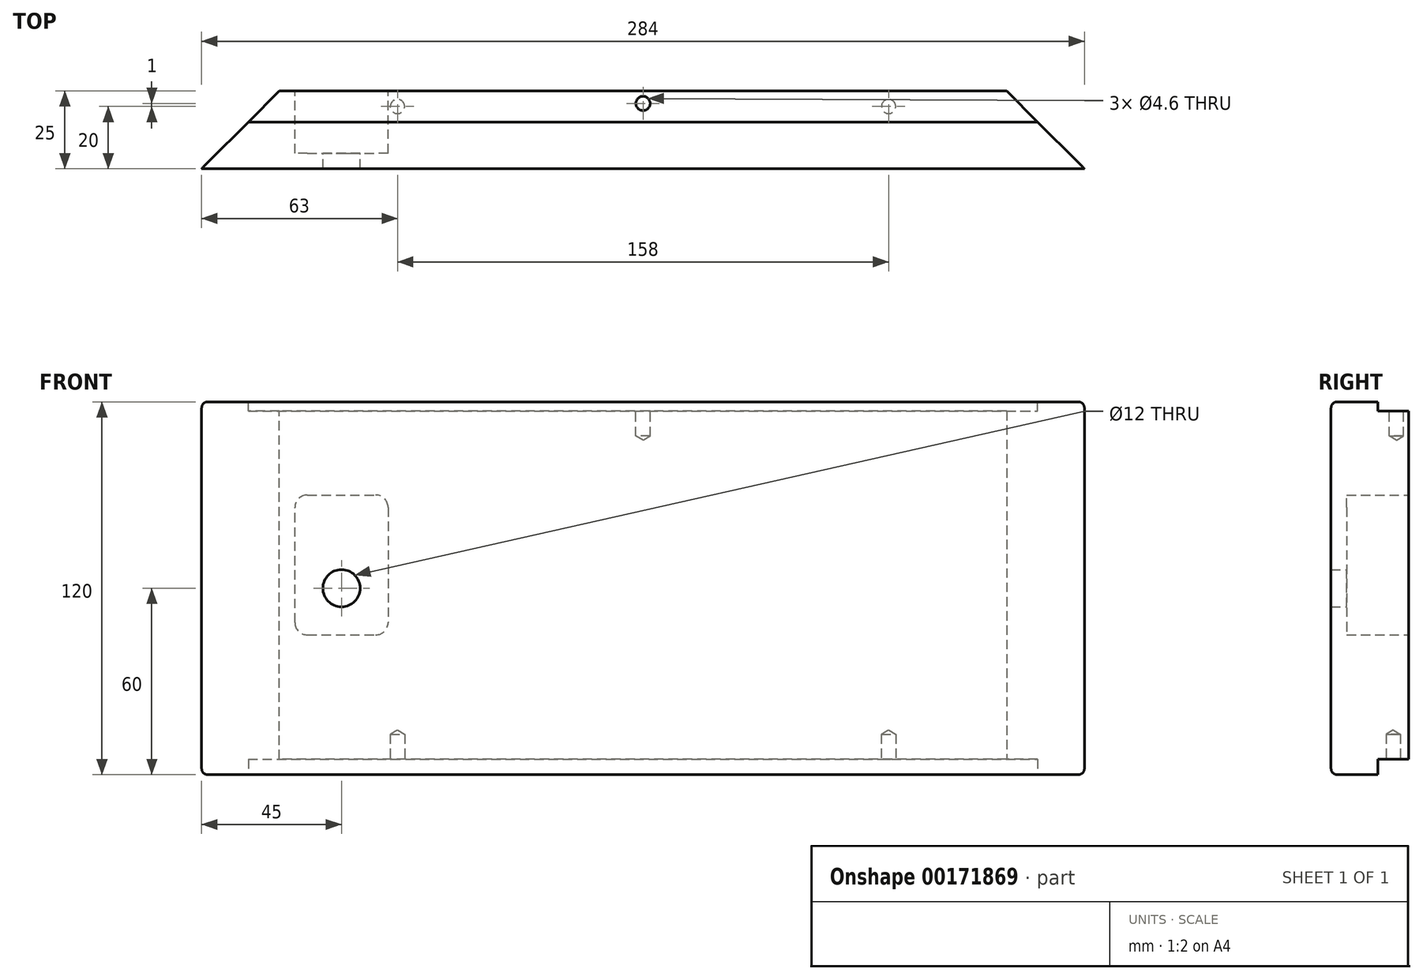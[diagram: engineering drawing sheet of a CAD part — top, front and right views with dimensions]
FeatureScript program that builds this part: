
annotation { "Feature Type Name" : "Feature", "Feature Type Description" : "" }
export const myFeature = defineFeature(function(context is Context, id is Id, definition is map)
    precondition{}
    {
        {
            var Q0;
            Q0=qCreatedBy(makeId("Front.planeOp"),FACE);
            var sketch = newSketch(context, id + "F0", { "sketchPlane" : qUnion([Q0])});
            skLineSegment(sketch, "E0.bottom", {"start": v(142, -60) * mm, "end": v(-142, -60) * mm});
            skLineSegment(sketch, "E0.top", {"start": v(142, 60) * mm, "end": v(-142, 60) * mm});
            skLineSegment(sketch, "E0.left", {"start": v(142, -60) * mm, "end": v(142, 60) * mm});
            skLineSegment(sketch, "E0.right", {"start": v(-142, -60) * mm, "end": v(-142, 60) * mm});
            skPoint(sketch, "E0.middle", {"position": v(0, 0) * mm});
            skLineSegment(sketch, "E1.right", {"start": v(-112, -11) * mm, "end": v(-112, 26) * mm});
            skLineSegment(sketch, "E2", {"start": v(-82, 26) * mm, "end": v(-82, -11) * mm});
            skLineSegment(sketch, "E3", {"start": v(-74.98, 0) * mm, "end": v(-115.97, 0) * mm, "construction": true});
            skLineSegment(sketch, "E4", {"start": v(-108, -15) * mm, "end": v(-86, -15) * mm});
            skLineSegment(sketch, "E5", {"start": v(-108, 30) * mm, "end": v(-86, 30) * mm});
            skPoint(sketch, "E6.visualSharp", {"position": v(-112, 30) * mm});
            skArc(sketch, "E6.filletArc", {"start": v(-108, 30) * mm, "mid": v(-110.83, 28.83) * mm, "end": v(-112, 26) * mm});
            skPoint(sketch, "E7.visualSharp", {"position": v(-82, 30) * mm});
            skArc(sketch, "E7.filletArc", {"start": v(-82, 26) * mm, "mid": v(-83.17, 28.83) * mm, "end": v(-86, 30) * mm});
            skPoint(sketch, "E8.visualSharp", {"position": v(-82, -15) * mm});
            skArc(sketch, "E8.filletArc", {"start": v(-86, -15) * mm, "mid": v(-83.17, -13.83) * mm, "end": v(-82, -11) * mm});
            skPoint(sketch, "E9.visualSharp", {"position": v(-112, -15) * mm});
            skArc(sketch, "E9.filletArc", {"start": v(-112, -11) * mm, "mid": v(-110.83, -13.83) * mm, "end": v(-108, -15) * mm});
            skLineSegment(sketch, "E10", {"start": v(-97, 45) * mm, "end": v(-97, -45) * mm, "construction": true});
            skLineSegment(sketch, "E11", {"start": v(-186.98, 0) * mm, "end": v(106.98, 0) * mm, "construction": true});
            skCircle(sketch, "E12", {"center": v(-97, 0) * mm, "radius": 6 * mm});
            skSolve(sketch);
        }
        {
            var Q0;
            Q0=makeQuery(id+"F0.imprint","IMPRINT",FACE,{"disambiguationData":[TD([[makeQuery(id+"F0.imprint","IMPRINT",EDGE,{"derivedFrom":sQuery(id+"F0.wireOp",EDGE,"E0.bottom")}),-1.0]])]});
            var Q1;
            Q1=makeQuery(id+"F0.imprint","IMPRINT",FACE,{"disambiguationData":[TD([[makeQuery(id+"F0.imprint","IMPRINT",EDGE,{"derivedFrom":sQuery(id+"F0.wireOp",EDGE,"E1.left")}),1.0]])]});
            var Q2;
            Q2=makeQuery(id+"F0.imprint","IMPRINT",FACE,{"disambiguationData":[TD([[makeQuery(id+"F0.imprint","IMPRINT",EDGE,{"derivedFrom":sQuery(id+"F0.wireOp",EDGE,"XVRcOiwa-wmZa-OlfB-imAZ-ZysaIvfTFvSH")}),1.0]])]});
            var Q3;
            Q3=makeQuery(id+"F0.imprint","IMPRINT",FACE,{"disambiguationData":[TD([[makeQuery(id+"F0.imprint","IMPRINT",EDGE,{"derivedFrom":sQuery(id+"F0.wireOp",EDGE,"492701c9-3a02-475b-877f-e4fc534a5983")}),1.0]])]});
            var Q4;
            Q4=makeQuery(id+"F0.imprint","IMPRINT",FACE,{"disambiguationData":[TD([[makeQuery(id+"F0.imprint","IMPRINT",EDGE,{"derivedFrom":sQuery(id+"F0.wireOp",EDGE,"E1.right")}),-1.0]])]});
            var Q5;
            {var subQ5=sQuery(id+"F0.wireOp",EDGE,"11b40b25-8dd5-4f7b-a4c1-55c3ff725173.left");Q5=makeQuery(id+"F0.imprint","IMPRINT",FACE,{"disambiguationData":[TD([[makeQuery(id+"F0.imprint","IMPRINT",EDGE,{"derivedFrom":subQ5}),1.0]])]});}
            var Q6;
            {var subQ0=sQuery(id+"F0.wireOp",EDGE,"050ddf37-6dd0-4eab-8f6c-0359ba11038c.filletArc");Q6=makeQuery(id+"F0.imprint","IMPRINT",FACE,{"disambiguationData":[TD([[makeQuery(id+"F0.imprint","IMPRINT",EDGE,{"derivedFrom":subQ0}),1.0]])]});}
            extrude(context, id + "F1", {"entities" : qUnion([Q0, Q1, Q2, Q3, Q4, Q5, Q6]), "depth" : 25 * mm});
        }
        {
            var Q0;
            Q0=makeQuery(id+"F1.opExtrude","CAP_EDGE",EDGE,{"disambiguationData":[OSD([sQuery(id+"F0.wireOp",EDGE,"E0.right")])],"isStart":true});
            var Q1;
            Q1=makeQuery(id+"F1.opExtrude","CAP_EDGE",EDGE,{"disambiguationData":[OSD([sQuery(id+"F0.wireOp",EDGE,"E0.left")])],"isStart":true});
            chamfer(context, id + "F2", {"entities" : qUnion([Q0, Q1]), "width" : 25 * mm, "tangentPropagation" : true});
        }
        {
            var Q0;
            Q0=makeQuery(id+"F1.opExtrude","SWEPT_FACE",FACE,{"disambiguationData":[OSD([sQuery(id+"F0.wireOp",EDGE,"E0.top")])]});
            var sketch = newSketch(context, id + "F3", { "sketchPlane" : qUnion([Q0])});
            skLineSegment(sketch, "E13", {"start": v(-127, -10) * mm, "end": v(127, -10) * mm});
            skLineSegment(sketch, "E14", {"start": v(-134.9, -4) * mm, "end": v(125.52, -4) * mm, "construction": true});
            skLineSegment(sketch, "E15", {"start": v(0, 10.75) * mm, "end": v(0, -16.45) * mm, "construction": true});
            skPoint(sketch, "E15.endSnap0", {"position": v(0, -10) * mm});
            skPoint(sketch, "E16", {"position": v(0, -4) * mm});
            skSolve(sketch);
        }
        {
            var Q0;
            {var subQ0=sQuery(id+"F3.wireOp",EDGE,"E13");Q0=makeQuery(id+"F3.imprint","IMPRINT",FACE,{"disambiguationData":[TD([[makeQuery(id+"F3.imprint","IMPRINT",EDGE,{"derivedFrom":subQ0}),1.0]])]});}
            extrude(context, id + "F4", {"entities" : qUnion([Q0]), "operationType" : NewBodyOperationType.REMOVE, "oppositeDirection" : true, "depth" : 3 * mm});
        }
        {
            var Q0;
            Q0=makeQuery(id+"F4.boolean.opBoolean","COPY",FACE,{"derivedFrom":makeQuery(id+"F4.opExtrude","CAP_FACE",FACE,{"disambiguationData":[OSD([sQuery(id+"F0.wireOp",EDGE,"E0.top"),sQuery(id+"F0.wireOp",EDGE,"E0.left"),sQuery(id+"F0.wireOp",EDGE,"E0.right"),sQuery(id+"F3.wireOp",EDGE,"E13")])],"isStart":false})});
            var sketch = newSketch(context, id + "F5", { "sketchPlane" : qUnion([Q0])});
            skLineSegment(sketch, "E17", {"start": v(-160.86, -4) * mm, "end": v(157.5, -4) * mm, "construction": true});
            skLineSegment(sketch, "E18", {"start": v(0, -19.46) * mm, "end": v(0, 5.76) * mm, "construction": true});
            skPoint(sketch, "E18.startSnap0", {"position": v(0, -10) * mm});
            skPoint(sketch, "E18.endSnap0", {"position": v(0, 0) * mm});
            skPoint(sketch, "E19", {"position": v(0, -4) * mm});
            skSolve(sketch);
        }
        {
            var Q0;
            Q0=sQuery(id+"F5.wireOp",VERTEX,"E19");
            var Q1;
            Q1=makeQuery(id+"F1.opExtrude","SWEPT_BODY",BODY,{"disambiguationData":[OSD([sQuery(id+"F0.wireOp",EDGE,"E0.bottom"),sQuery(id+"F0.wireOp",EDGE,"E0.top"),sQuery(id+"F0.wireOp",EDGE,"E0.left"),sQuery(id+"F0.wireOp",EDGE,"E0.right"),sQuery(id+"F0.wireOp",EDGE,"OmMS4I8q-v5Nw-sNs6-rLWv-C37PQFSncukl.bottom"),sQuery(id+"F0.wireOp",EDGE,"OmMS4I8q-v5Nw-sNs6-rLWv-C37PQFSncukl.top"),sQuery(id+"F0.wireOp",EDGE,"OmMS4I8q-v5Nw-sNs6-rLWv-C37PQFSncukl.left"),sQuery(id+"F0.wireOp",EDGE,"OmMS4I8q-v5Nw-sNs6-rLWv-C37PQFSncukl.right"),sQuery(id+"F0.wireOp",EDGE,"a599c4f8-9d5b-4f08-a6f5-21f0fa9e66a0.filletArc"),sQuery(id+"F0.wireOp",EDGE,"32fc2319-0cb2-45e8-9aa6-fcf55b2109a0.filletArc"),sQuery(id+"F0.wireOp",EDGE,"258bbff2-458d-4a09-ab05-362c01f2241a.filletArc"),sQuery(id+"F0.wireOp",EDGE,"b6ee52c4-7d80-4818-82dd-608125603be5.filletArc")])]});
            hole(context, id + "F6", {"style" : HoleStyle.SIMPLE, "endStyle" : HoleEndStyle.BLIND, "holeDiameter" : 4.6 * mm, "holeDepth" : 8 * mm, "startFromSketch" : true, "locations" : qUnion([Q0]), "scope" : qUnion([Q1])});
        }
        {
            var Q0;
            Q0=makeQuery(id+"F1.opExtrude","SWEPT_FACE",FACE,{"disambiguationData":[OSD([sQuery(id+"F0.wireOp",EDGE,"E0.bottom")])]});
            var sketch = newSketch(context, id + "F7", { "sketchPlane" : qUnion([Q0])});
            skLineSegment(sketch, "E20", {"start": v(-127, 10) * mm, "end": v(127, 10) * mm});
            skSolve(sketch);
        }
        {
            var Q0;
            {var subQ0=sQuery(id+"F7.wireOp",EDGE,"E20");Q0=makeQuery(id+"F7.imprint","IMPRINT",FACE,{"disambiguationData":[TD([[makeQuery(id+"F7.imprint","IMPRINT",EDGE,{"derivedFrom":subQ0}),-1.0]])]});}
            extrude(context, id + "F8", {"entities" : qUnion([Q0]), "operationType" : NewBodyOperationType.REMOVE, "oppositeDirection" : true, "depth" : 5 * mm});
        }
        {
            var Q0;
            Q0=makeQuery(id+"F8.boolean.opBoolean","COPY",FACE,{"derivedFrom":makeQuery(id+"F8.opExtrude","CAP_FACE",FACE,{"disambiguationData":[OSD([sQuery(id+"F0.wireOp",EDGE,"E0.bottom"),sQuery(id+"F0.wireOp",EDGE,"E0.left"),sQuery(id+"F0.wireOp",EDGE,"E0.right"),sQuery(id+"F7.wireOp",EDGE,"E20")])],"isStart":false})});
            var sketch = newSketch(context, id + "F9", { "sketchPlane" : qUnion([Q0])});
            skLineSegment(sketch, "E21", {"start": v(-269.27, 5) * mm, "end": v(258.64, 5) * mm, "construction": true});
            skLineSegment(sketch, "E22", {"start": v(-79, 26.7) * mm, "end": v(-79, -18.52) * mm, "construction": true});
            skLineSegment(sketch, "E23", {"start": v(79, 29.82) * mm, "end": v(79, -15.76) * mm, "construction": true});
            skPoint(sketch, "E24", {"position": v(-79, 5) * mm});
            skPoint(sketch, "E25", {"position": v(79, 5) * mm});
            skPoint(sketch, "E26", {"position": v(0, 5) * mm});
            skSolve(sketch);
        }
        {
            var Q0;
            Q0=sQuery(id+"F9.wireOp",VERTEX,"E24");
            var Q1;
            Q1=sQuery(id+"F9.wireOp",VERTEX,"E25");
            var Q2;
            Q2=makeQuery(id+"F1.opExtrude","SWEPT_BODY",BODY,{"disambiguationData":[OSD([sQuery(id+"F0.wireOp",EDGE,"E0.bottom"),sQuery(id+"F0.wireOp",EDGE,"E0.top"),sQuery(id+"F0.wireOp",EDGE,"E0.left"),sQuery(id+"F0.wireOp",EDGE,"E0.right"),sQuery(id+"F0.wireOp",EDGE,"OmMS4I8q-v5Nw-sNs6-rLWv-C37PQFSncukl.bottom"),sQuery(id+"F0.wireOp",EDGE,"OmMS4I8q-v5Nw-sNs6-rLWv-C37PQFSncukl.top"),sQuery(id+"F0.wireOp",EDGE,"OmMS4I8q-v5Nw-sNs6-rLWv-C37PQFSncukl.left"),sQuery(id+"F0.wireOp",EDGE,"OmMS4I8q-v5Nw-sNs6-rLWv-C37PQFSncukl.right"),sQuery(id+"F0.wireOp",EDGE,"a599c4f8-9d5b-4f08-a6f5-21f0fa9e66a0.filletArc"),sQuery(id+"F0.wireOp",EDGE,"32fc2319-0cb2-45e8-9aa6-fcf55b2109a0.filletArc"),sQuery(id+"F0.wireOp",EDGE,"258bbff2-458d-4a09-ab05-362c01f2241a.filletArc"),sQuery(id+"F0.wireOp",EDGE,"b6ee52c4-7d80-4818-82dd-608125603be5.filletArc")])]});
            hole(context, id + "F10", {"style" : HoleStyle.SIMPLE, "endStyle" : HoleEndStyle.BLIND, "holeDiameter" : 4.6 * mm, "holeDepth" : 8 * mm, "startFromSketch" : true, "locations" : qUnion([Q0, Q1]), "scope" : qUnion([Q2])});
        }
        {
            var Q0;
            Q0=makeQuery(id+"F1.opExtrude","CAP_EDGE",EDGE,{"disambiguationData":[OSD([sQuery(id+"F0.wireOp",EDGE,"E0.top")])],"isStart":false});
            var Q1;
            Q1=makeQuery(id+"F1.opExtrude","CAP_EDGE",EDGE,{"disambiguationData":[OSD([sQuery(id+"F0.wireOp",EDGE,"E0.bottom")])],"isStart":false});
            fillet(context, id + "F11", {"entities" : qUnion([Q0, Q1]), "radius" : 2 * mm, "tangentPropagation" : true, "allowEdgeOverflow" : false});
        }
        {
            var Q0;
            Q0=makeQuery(id+"F0.imprint","IMPRINT",FACE,{"disambiguationData":[TD([[makeQuery(id+"F0.imprint","IMPRINT",EDGE,{"derivedFrom":sQuery(id+"F0.wireOp",EDGE,"E1.left")}),1.0]])]});
            var Q1;
            Q1=makeQuery(id+"F0.imprint","IMPRINT",FACE,{"disambiguationData":[TD([[makeQuery(id+"F0.imprint","IMPRINT",EDGE,{"derivedFrom":sQuery(id+"F0.wireOp",EDGE,"XVRcOiwa-wmZa-OlfB-imAZ-ZysaIvfTFvSH")}),1.0]])]});
            var Q2;
            Q2=makeQuery(id+"F0.imprint","IMPRINT",FACE,{"disambiguationData":[TD([[makeQuery(id+"F0.imprint","IMPRINT",EDGE,{"derivedFrom":sQuery(id+"F0.wireOp",EDGE,"492701c9-3a02-475b-877f-e4fc534a5983")}),1.0]])]});
            var Q3;
            Q3=makeQuery(id+"F0.imprint","IMPRINT",FACE,{"disambiguationData":[TD([[makeQuery(id+"F0.imprint","IMPRINT",EDGE,{"derivedFrom":sQuery(id+"F0.wireOp",EDGE,"E1.right")}),-1.0]])]});
            var Q4;
            {var subQ5=sQuery(id+"F0.wireOp",EDGE,"11b40b25-8dd5-4f7b-a4c1-55c3ff725173.left");Q4=makeQuery(id+"F0.imprint","IMPRINT",FACE,{"disambiguationData":[TD([[makeQuery(id+"F0.imprint","IMPRINT",EDGE,{"derivedFrom":subQ5}),1.0]])]});}
            var Q5;
            {var subQ0=sQuery(id+"F0.wireOp",EDGE,"050ddf37-6dd0-4eab-8f6c-0359ba11038c.filletArc");Q5=makeQuery(id+"F0.imprint","IMPRINT",FACE,{"disambiguationData":[TD([[makeQuery(id+"F0.imprint","IMPRINT",EDGE,{"derivedFrom":subQ0}),1.0]])]});}
            extrude(context, id + "F12", {"entities" : qUnion([Q0, Q1, Q2, Q3, Q4, Q5]), "operationType" : NewBodyOperationType.REMOVE, "depth" : 20 * mm});
        }
    });
